# Revit family: LAMP_FIL 45 1680MM TECH SUSPENDED
name_source: partatom
category: Luminarias
revit_build: Autodesk Revit 2018 (Build: 20170223_1515(x64)
units: mm (PartAtom-declared; Revit-internal decimal feet)

## family parameters
Anfitrión = Cara
Compartido = No
Corte con vacíos al cargar = No
Cota de conector redondo = Diámetro de uso
Origen de luz = Sí
Punto de cálculo de habitación = No
Tipo de pieza = Normal

## types (12) — shared parameters
CRI = 80
Cambio de temperatura de color de luz atenuada = <Ninguno>
Dimensions = 1680x45x80
Elevación por defecto = 1219 mm
Fabricante = LAMP
Filtro de color = 16777215
Gear = Electronic
IEE = A+
Installation instructions = https://www.lamp.es
Insulation class = I
LED Lifetime = 70.000 L80 B10
Lamp = MID-POWER LED
Last update = 19/03/2021
Longitud de línea de emisión = 1680 mm  [stored 5.51181 ft]
MacAdam = 3
Manufacturer URL = http://www.lamp.es
Manufacturer country = Spain
Manufacturer name = LAMP
Material difusor = LAMP_PC Difusor Opal Fil
Material suspension = LAMP_Acero genérico
Plum = 25 W
Power = 23 W
Power Supply = 220-240V 50/60Hz
Product URL = https://www.lamp.es
Product datasheet = http://www.lamp.es
Protection rating = IP20 / IK07
Type = MID POWER TRIDONIC
Ángulo de inclinación = -90.00°

## per-type parameters (varying)
| type | Archivo de red fotométrica | Descripción | Efficacy | Finish | Material perfil | Modelo | Product code | Weight |
| 3900LM 3000K DALI BLACK | F41SF168MOTE830nB.IES | FIL45 SUR 1680 3900 WW TECH DALI BK. | 114 lm/W | Matte black RAL 9011 | LAMP_Aluminio Perfil Fil NG | F41SF168MOTE830DB | F41SF168MOTE830DB | 3.83 kg |
| 3900LM 3000K DALI GREY | F41SF168MOTE830nG.IES | FIL45 SUR 1680 3900 WW TECH DALI GR. | 114 lm/W | Gloss grey | LAMP_Aluminio Perfil Fil GR | F41SF168MOTE830DG | F41SF168MOTE830DG | 3.83 kg |
| 3900LM 3000K DALI WHITE | F41SF168MOTE830nW.IES | FIL45 SUR 1680 3900 WW TECH DALI WH. | 114 lm/W | Matte white RAL 9010 | LAMP_Aluminio Perfil Fil BL | F41SF168MOTE830DW | F41SF168MOTE830DW | 3.83 kg |
| 3900LM 3000K  BLACK | F41SF168MOTE830NB.IES | FIL45 SUR 1680 3900 WW TECH BK. | 114 lm/W | Matte black RAL 9011 | LAMP_Aluminio Perfil Fil NG | F41SF168MOTE830NB | F41SF168MOTE830NB | 3.63 kg |
| 3900LM 3000K  GREY | F41SF168MOTE830NG.IES | FIL45 SUR 1680 3900 WW TECH GR. | 114 lm/W | Gloss grey | LAMP_Aluminio Perfil Fil GR | F41SF168MOTE830NG | F41SF168MOTE830NG | 3.63 kg |
| 3900LM 3000K  WHITE | F41SF168MOTE830NW.IES | FIL45 SUR 1680 3900 WW TECH WH. | 114 lm/W | Matte white RAL 9010 | LAMP_Aluminio Perfil Fil BL | F41SF168MOTE830NW | F41SF168MOTE830NW | 3.63 kg |
| 3900LM 4000K DALI BLACK | F41SF168MOTE840nB.IES | FIL45 SUR 1680 3900 NW TECH DALI BK. | 119 lm/W | Matte black RAL 9011 | LAMP_Aluminio Perfil Fil NG | F41SF168MOTE840DB | F41SF168MOTE840DB | 3.83 kg |
| 3900LM 4000K DALI GREY | F41SF168MOTE840nG.IES | FIL45 SUR 1680 3900 NW TECH DALI GR. | 119 lm/W | Gloss grey | LAMP_Aluminio Perfil Fil GR | F41SF168MOTE840DG | F41SF168MOTE840DG | 3.83 kg |
| 3900LM 4000K DALI WHITE | F41SF168MOTE840nW.IES | FIL45 SUR 1680 3900 NW TECH DALI WH. | 119 lm/W | Matte white RAL 9010 | LAMP_Aluminio Perfil Fil BL | F41SF168MOTE840DW | F41SF168MOTE840DW | 3.83 kg |
| 3900LM 4000K  BLACK | F41SF168MOTE840NB.IES | FIL45 SUR 1680 3900 NW TECH BK. | 119 lm/W | Matte black RAL 9011 | LAMP_Aluminio Perfil Fil NG | F41SF168MOTE840NB | F41SF168MOTE840NB | 3.63 kg |
| 3900LM 4000K  GREY | F41SF168MOTE840NG.IES | FIL45 SUR 1680 3900 NW TECH GR. | 119 lm/W | Gloss grey | LAMP_Aluminio Perfil Fil GR | F41SF168MOTE840NG | F41SF168MOTE840NG | 3.63 kg |
| 3900LM 4000K  WHITE | F41SF168MOTE840NW.IES | FIL45 SUR 1680 3900 NW TECH WH. | 119 lm/W | Matte white RAL 9010 | LAMP_Aluminio Perfil Fil BL | F41SF168MOTE840NW | F41SF168MOTE840NW | 3.63 kg |

note: [stored X ft] marks values corroborated as IEEE doubles in the binary element streams (Revit-internal decimal feet)
